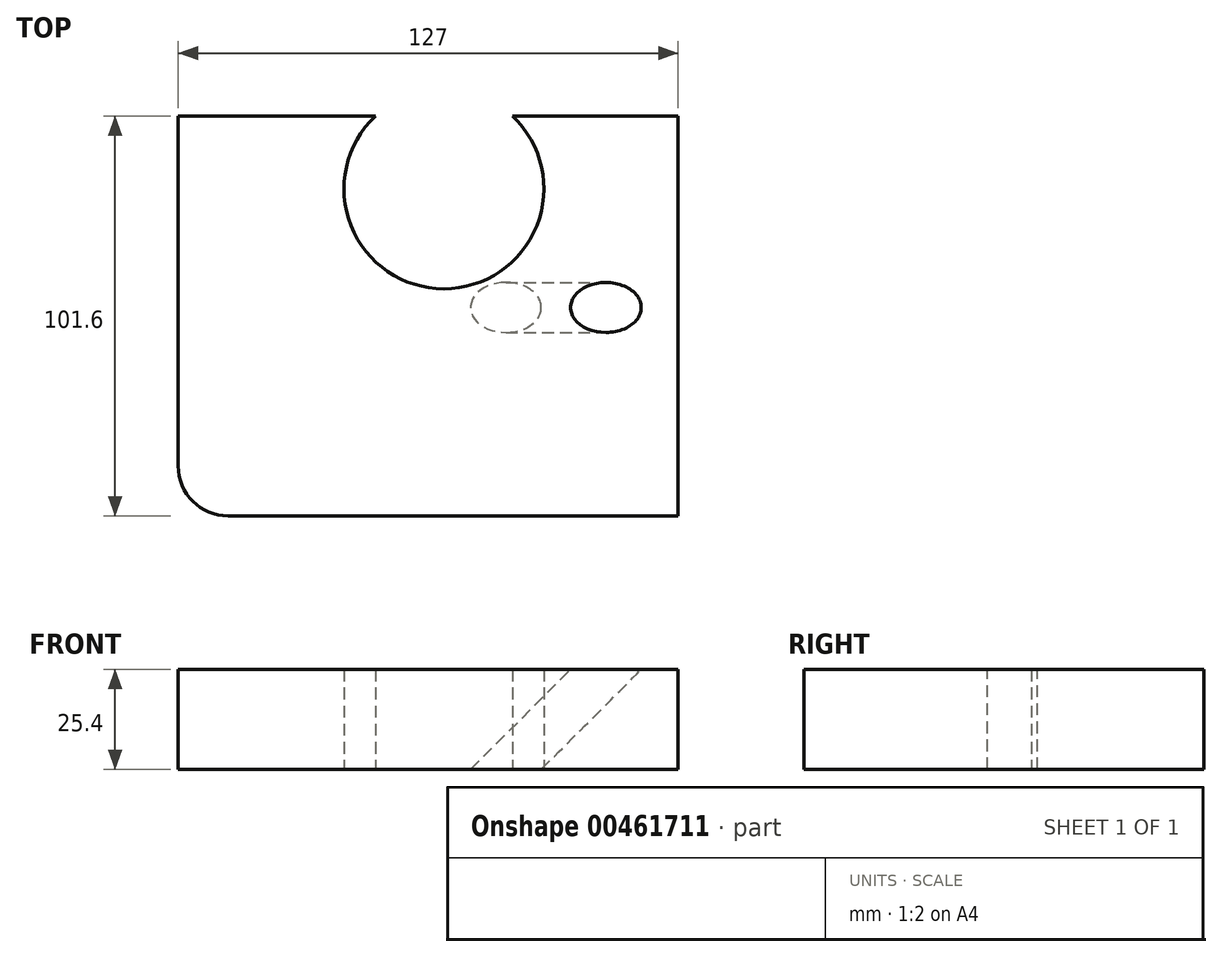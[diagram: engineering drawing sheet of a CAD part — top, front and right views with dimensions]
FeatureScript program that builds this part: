
annotation { "Feature Type Name" : "Feature", "Feature Type Description" : "" }
export const myFeature = defineFeature(function(context is Context, id is Id, definition is map)
    precondition{}
    {
        {
            var Q0;
            Q0=qCreatedBy(makeId("Top.planeOp"),FACE);
            var sketch = newSketch(context, id + "F0", { "sketchPlane" : qUnion([Q0])});
            skLineSegment(sketch, "E0.bottom", {"start": v(-67.5, 21.28) * mm, "end": v(-17.42, 21.28) * mm});
            skLineSegment(sketch, "E0.top", {"start": v(-54.8, -80.32) * mm, "end": v(59.5, -80.32) * mm});
            skLineSegment(sketch, "E0.left", {"start": v(-67.5, 21.28) * mm, "end": v(-67.5, -67.62) * mm});
            skLineSegment(sketch, "E0.right", {"start": v(59.5, 21.28) * mm, "end": v(59.5, -80.32) * mm});
            skCircle(sketch, "E1", {"center": v(0, 2.8) * mm, "radius": 25.4 * mm});
            skLineSegment(sketch, "E2.trimOffspring", {"start": v(17.42, 21.28) * mm, "end": v(59.5, 21.28) * mm});
            skPoint(sketch, "E3.visualSharp", {"position": v(-67.5, -80.32) * mm});
            skArc(sketch, "E3.filletArc", {"start": v(-67.5, -67.62) * mm, "mid": v(-63.78, -76.6) * mm, "end": v(-54.8, -80.32) * mm});
            skSolve(sketch);
        }
        {
            var Q0;
            {var subQ0=sQuery(id+"F0.wireOp",EDGE,"E0.bottom");Q0=makeQuery(id+"F0.imprint","IMPRINT",FACE,{"disambiguationData":[TD([[makeQuery(id+"F0.imprint","IMPRINT",EDGE,{"derivedFrom":subQ0}),-1.0]])]});}
            extrude(context, id + "F1", {"entities" : qUnion([Q0]), "depth" : 25.4 * mm});
        }
        {
            var Q0;
            Q0=makeQuery(id+"F1.opExtrude","CAP_EDGE",EDGE,{"disambiguationData":[OSD([sQuery(id+"F0.wireOp",EDGE,"E0.right")])],"isStart":false});
            cPlane(context, id + "F2", {"entities" : qUnion([Q0]), "cplaneType" : CPlaneType.LINE_ANGLE, "offset" : 25.4 * mm, "angle" : 45 * degree, "oppositeDirection" : true, "width" : 152.4 * mm, "height" : 152.4 * mm});
        }
        {
            var Q0;
            Q0=qCreatedBy(id+"F2.planeOp",FACE);
            var sketch = newSketch(context, id + "F3", { "sketchPlane" : qUnion([Q0])});
            skCircle(sketch, "E4", {"center": v(27.35, -11.14) * mm, "radius": 6.35 * mm});
            skSolve(sketch);
        }
        {
            var Q0;
            Q0=makeQuery(id+"F3.imprint","IMPRINT",FACE,{"disambiguationData":[TD([[makeQuery(id+"F3.imprint","IMPRINT",EDGE,{"derivedFrom":sQuery(id+"F3.wireOp",EDGE,"E4")}),1.0]])]});
            extrude(context, id + "F4", {"entities" : qUnion([Q0]), "operationType" : NewBodyOperationType.REMOVE, "depth" : 127 * mm});
        }
    });
